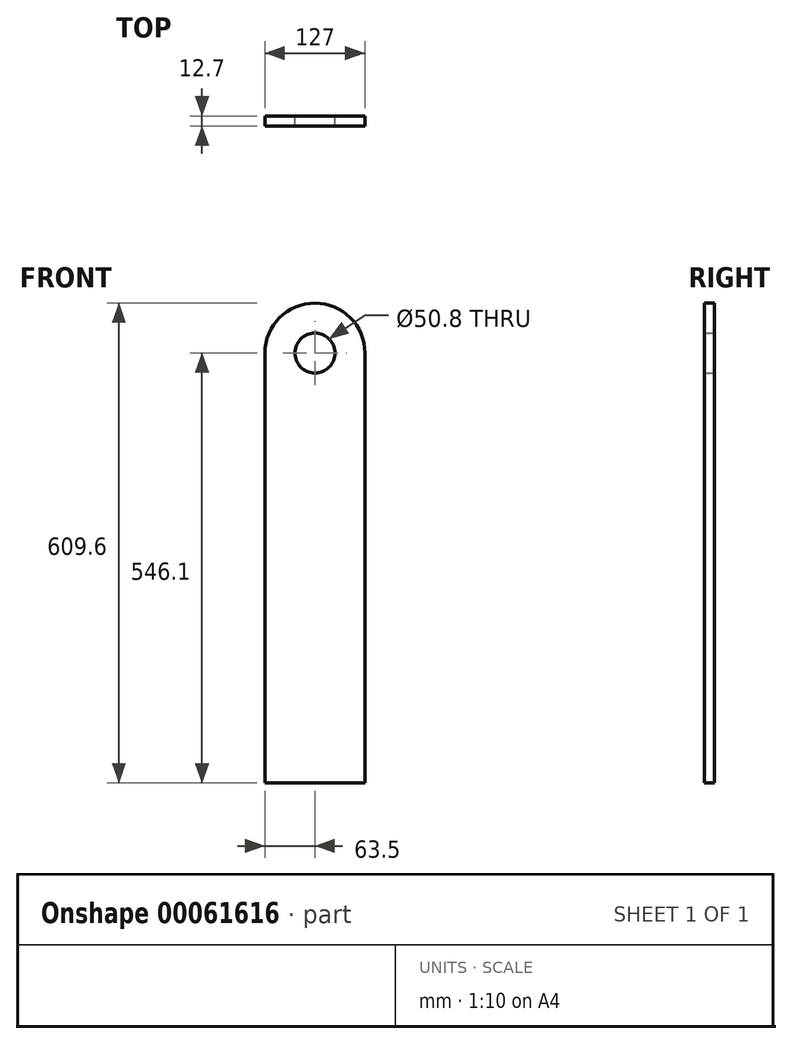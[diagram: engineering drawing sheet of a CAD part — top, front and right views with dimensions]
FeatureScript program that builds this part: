
annotation { "Feature Type Name" : "Feature", "Feature Type Description" : "" }
export const myFeature = defineFeature(function(context is Context, id is Id, definition is map)
    precondition{}
    {
        {
            var Q0;
            Q0=qCreatedBy(makeId("Front.planeOp"),FACE);
            var sketch = newSketch(context, id + "F0", { "sketchPlane" : qUnion([Q0])});
            skLineSegment(sketch, "E0.rect.top", {"start": v(-63.5, -273.05) * mm, "end": v(63.5, -273.05) * mm});
            skLineSegment(sketch, "E0.rect.left", {"start": v(-63.5, 273.05) * mm, "end": v(-63.5, -273.05) * mm});
            skLineSegment(sketch, "E0.rect.right", {"start": v(63.5, 273.05) * mm, "end": v(63.5, -273.05) * mm});
            skPoint(sketch, "E0.rect.middle", {"position": v(0, 0) * mm});
            skArc(sketch, "E1", {"start": v(63.5, 273.05) * mm, "mid": v(0, 336.55) * mm, "end": v(-63.5, 273.05) * mm});
            skCircle(sketch, "E2", {"center": v(0, 273.05) * mm, "radius": 25.4 * mm});
            skSolve(sketch);
        }
        {
            var Q0;
            Q0=makeQuery(id+"F0.imprint","IMPRINT",FACE,{"disambiguationData":[TD([[makeQuery(id+"F0.imprint","IMPRINT",EDGE,{"derivedFrom":sQuery(id+"F0.wireOp",EDGE,"E0.rect.top")}),1.0]])]});
            extrude(context, id + "F1", {"entities" : qUnion([Q0]), "depth" : 12.7 * mm});
        }
    });
